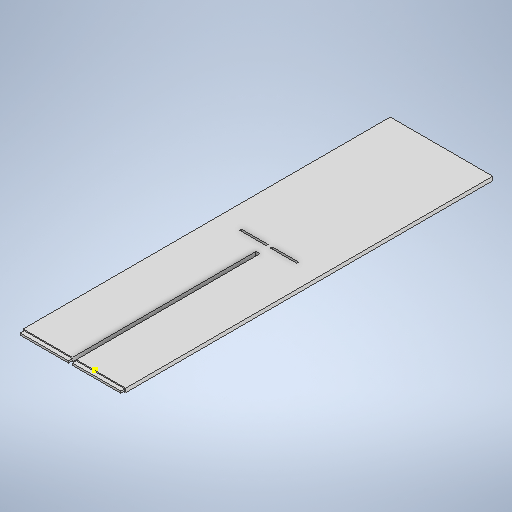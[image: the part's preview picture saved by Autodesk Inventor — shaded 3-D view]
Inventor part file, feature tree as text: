
AUTODESK INVENTOR PART (.ipt)
format: ipt  version: 2025.2 (Build 292293000, 293)  size: 403,968 bytes
history: native  units: mm
features: sketch x15, extrude x14, projected_geometry x3
ambient origin geometry x8: Origin, YZ Plane, XZ Plane, XY Plane, X Axis, Y Axis, Z Axis, Center Point
bodies: Solid1 (feature_tree)
feature tree (32):
  extrude  "Extrusion1"  Depth=447.675mm
  extrude  "Extrusion2"  Depth=4.7625mm TaperAngle=0.0deg
  extrude  "Extrusion3"  Depth=10.0mm TaperAngle=0.0deg
  extrude  "Extrusion4"  Depth=158.838mm TaperAngle=0.0deg
  sketch  "Sketch5"  dims[d25=4.763mm d26=223.837mm d27=0.0mm]
  extrude  "Extrusion5"  Depth=223.837mm TaperAngle=0.0deg
  extrude  "Extrusion6"  Depth=15.0mm TaperAngle=0.0deg
  extrude  "Extrusion7"  Depth=2.374mm TaperAngle=0.0deg
  extrude  "Extrusion8"  Depth=2.374mm TaperAngle=0.0deg
  extrude  "Extrusion9"  Depth=4.763mm
  extrude  "Extrusion10"  Depth=10.0mm TaperAngle=0.0deg
  extrude  "Extrusion11"  Depth=10.0mm TaperAngle=0.0deg
  extrude  "Extrusion12"  [1 undecoded]
  extrude  "Extrusion13"  [1 undecoded]
  extrude  "Extrusion14"  [1 undecoded]
  sketch  "Sketch1"  dims[d0=50.0mm d1=447.675mm]
  sketch  "Sketch2"  dims[d2=4.7625mm d3=0.0mm d9=4.7625mm d10=0.0mm]
  sketch  "Sketch3"  dims[d11=25.0mm d18=10.0mm d19=0.0mm]
  sketch  "Sketch4"  dims[d20=10.0mm d21=0.0mm d22=158.838mm d23=0.0mm]
  sketch  "Sketch6"  dims[d28=15.0mm d29=0.0mm d30=15.0mm d31=0.0mm]
  projected_geometry  "Projected Loop1"
  sketch  "Sketch8"  dims[d35=2.374mm d36=10.0mm d37=0.0mm]
  sketch  "Sketch9"  dims[d43=2.374mm d44=10.0mm d45=0.0mm]
  projected_geometry  "Projected Loop2"
  sketch  "Sketch10"  dims[d46=4.763mm d47=0.0mm d48=37.5mm]
  projected_geometry  "Projected Loop3"
  sketch  "Sketch14"  dims[d49=37.5mm d50=10.0mm d51=0.0mm]
  sketch  "Sketch17"  dims[d53=10.0mm d54=0.0mm d57=10.0mm d58=0.0mm]
  sketch  "Sketch18"
  sketch  "Sketch19"
  sketch  "Sketch20"
  sketch  "Sketch21"
note: 3 required parameter values undecoded (feature->parameter linkage not recoverable at this tier; creation-order binding heuristic only, values carry confidence <= 0.55)
